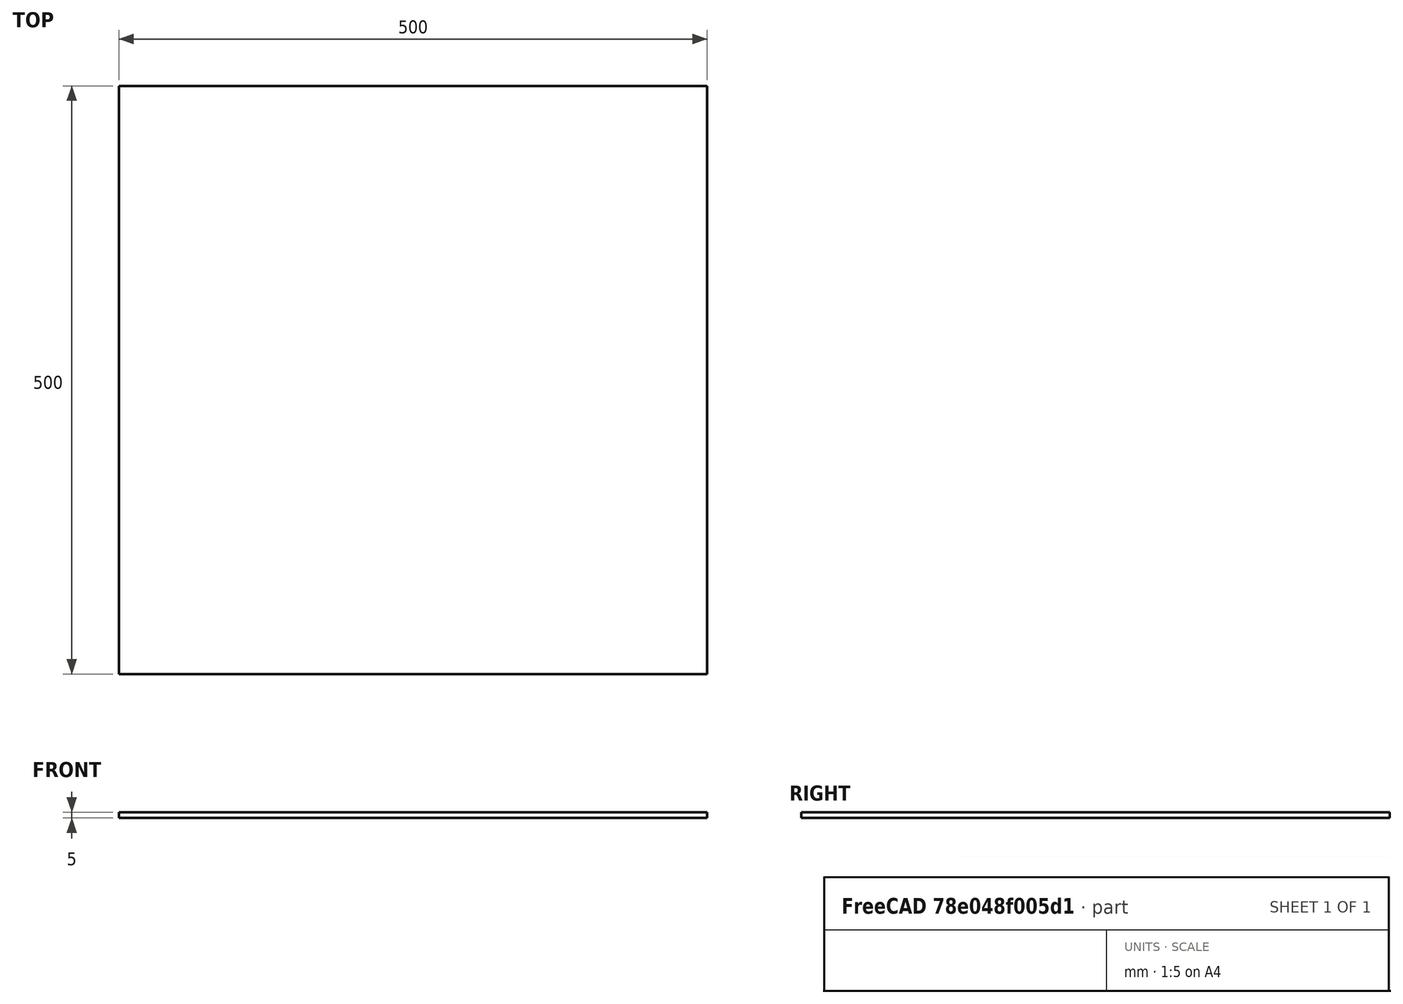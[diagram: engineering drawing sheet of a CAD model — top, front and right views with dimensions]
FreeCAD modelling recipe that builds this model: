
FCSTD DOCUMENT  (FreeCAD 0.17RUnknown)
Label: empty_small_table
License: All rights reserved
LicenseURL: http://en.wikipedia.org/wiki/All_rights_reserved
objects: Sketcher::SketchObject×1, PartDesign::Pad×1, PartDesign::Body×1
note: 4 computed .brp shape members not serialized (recipe doc carries the construction recipe); baked Part::Feature solids carry a one-line shape summary decoded from their .brp

FEATURE [Sketcher::SketchObject] Sketch
  MapMode = 5
  Support = -> [XY_Plane]
  sketch-geometry (4):
    g0: LineSegment StartX=0 StartY=0 StartZ=0 EndX=500 EndY=0 EndZ=0
    g1: LineSegment StartX=500 StartY=0 StartZ=0 EndX=500 EndY=500 EndZ=0
    g2: LineSegment StartX=500 StartY=500 StartZ=0 EndX=0 EndY=500 EndZ=0
    g3: LineSegment StartX=0 StartY=500 StartZ=0 EndX=0 EndY=0 EndZ=0
  constraints (11):
    c: Coincident(g0,g1)
    c: Coincident(g1,g2)
    c: Coincident(g2,g3)
    c: Coincident(g3,g0)
    c: Horizontal(g0)
    c: Horizontal(g2)
    c: Vertical(g1)
    c: Vertical(g3)
    c: Coincident(g0,g-1)
    c: DistanceX(g0,g0) = 500
    c: DistanceY(g3,g3) = 500
FEATURE [PartDesign::Pad] Pad
  Length = 5
  Length2 = 100
  Profile = -> Sketch
  Type = 0
FEATURE [PartDesign::Body] Body
  Group = -> [Sketch,Pad]
  Origin = -> Origin
  Tip = -> Pad
